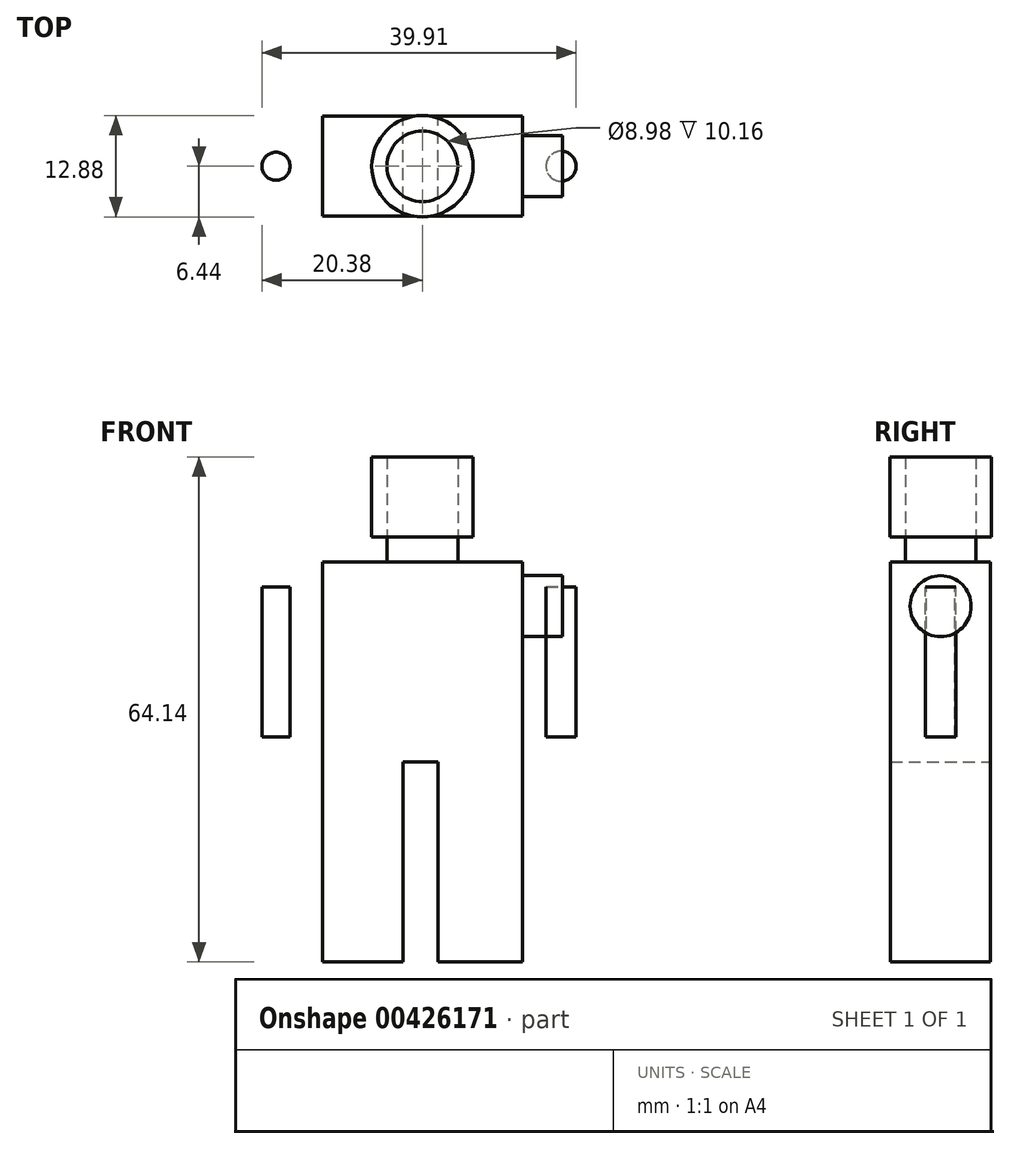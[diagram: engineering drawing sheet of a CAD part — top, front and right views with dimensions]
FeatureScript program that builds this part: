
annotation { "Feature Type Name" : "Feature", "Feature Type Description" : "" }
export const myFeature = defineFeature(function(context is Context, id is Id, definition is map)
    precondition{}
    {
        {
            var Q0;
            Q0=qCreatedBy(makeId("Top.planeOp"),FACE);
            var sketch = newSketch(context, id + "F0", { "sketchPlane" : qUnion([Q0])});
            skLineSegment(sketch, "E0.bottom", {"start": v(0, 0) * mm, "end": v(-12.7, 0) * mm});
            skLineSegment(sketch, "E0.top", {"start": v(0, -6.35) * mm, "end": v(-12.7, -6.35) * mm});
            skLineSegment(sketch, "E0.left", {"start": v(0, 0) * mm, "end": v(0, -6.35) * mm});
            skLineSegment(sketch, "E0.right", {"start": v(-12.7, 0) * mm, "end": v(-12.7, -6.35) * mm});
            skLineSegment(sketch, "E1.top", {"start": v(0, 6.35) * mm, "end": v(-12.7, 6.35) * mm});
            skLineSegment(sketch, "E1.left", {"start": v(0, 0) * mm, "end": v(0, 6.35) * mm});
            skLineSegment(sketch, "E1.right", {"start": v(-12.7, 0) * mm, "end": v(-12.7, 6.35) * mm});
            skLineSegment(sketch, "E2.bottom", {"start": v(0, -6.35) * mm, "end": v(12.7, -6.35) * mm});
            skLineSegment(sketch, "E2.top", {"start": v(0, 0) * mm, "end": v(12.7, 0) * mm});
            skLineSegment(sketch, "E2.left", {"start": v(0, -6.35) * mm, "end": v(0, 0) * mm});
            skLineSegment(sketch, "E2.right", {"start": v(12.7, -6.35) * mm, "end": v(12.7, 0) * mm});
            skLineSegment(sketch, "E3.top", {"start": v(0, 6.35) * mm, "end": v(12.7, 6.35) * mm});
            skLineSegment(sketch, "E3.right", {"start": v(12.7, 0) * mm, "end": v(12.7, 6.35) * mm});
            skSolve(sketch);
        }
        {
            var Q0;
            Q0 = qSketchRegion(id + "F0", true);
            extrude(context, id + "F1", {"entities" : qUnion([Q0]), "endBound" : BoundingType.SYMMETRIC, "depth" : 25.4 * mm});
        }
        {
            var Q0;
            Q0=makeQuery(id+"F1.opExtrude","CAP_FACE",FACE,{"disambiguationData":[OSD([sQuery(id+"F0.wireOp",EDGE,"E0.top"),sQuery(id+"F0.wireOp",EDGE,"E0.right"),sQuery(id+"F0.wireOp",EDGE,"E1.top"),sQuery(id+"F0.wireOp",EDGE,"E1.right"),sQuery(id+"F0.wireOp",EDGE,"E2.bottom"),sQuery(id+"F0.wireOp",EDGE,"E2.right"),sQuery(id+"F0.wireOp",EDGE,"E3.top"),sQuery(id+"F0.wireOp",EDGE,"E3.right")])],"isStart":false});
            var sketch = newSketch(context, id + "F2", { "sketchPlane" : qUnion([Q0])});
            skCircle(sketch, "E4", {"center": v(0, 0) * mm, "radius": 4.5 * mm});
            skSolve(sketch);
        }
        {
            var Q0;
            Q0=makeQuery(id+"F2.imprint","IMPRINT",FACE,{"disambiguationData":[TD([[makeQuery(id+"F2.imprint","IMPRINT",EDGE,{"derivedFrom":sQuery(id+"F2.wireOp",EDGE,"E4")}),1.0]])]});
            extrude(context, id + "F3", {"entities" : qUnion([Q0]), "operationType" : NewBodyOperationType.ADD, "endBound" : BoundingType.SYMMETRIC, "depth" : 6.35 * mm});
        }
        {
            var Q0;
            Q0=makeQuery(id+"F3.opExtrude","CAP_FACE",FACE,{"disambiguationData":[OSD([sQuery(id+"F2.wireOp",EDGE,"E4")])],"isStart":false});
            var sketch = newSketch(context, id + "F4", { "sketchPlane" : qUnion([Q0])});
            skCircle(sketch, "E5", {"center": v(0, 0) * mm, "radius": 6.44 * mm});
            skSolve(sketch);
        }
        {
            var Q0;
            Q0=makeQuery(id+"F4.imprint","IMPRINT",FACE,{"disambiguationData":[TD([[makeQuery(id+"F4.imprint","IMPRINT",EDGE,{"derivedFrom":sQuery(id+"F4.wireOp",EDGE,"E5")}),1.0]])]});
            extrude(context, id + "F5", {"entities" : qUnion([Q0]), "depth" : 10.16 * mm});
        }
        {
            var Q0;
            Q0=makeQuery(id+"F1.opExtrude","SWEPT_FACE",FACE,{"disambiguationData":[OSD([sQuery(id+"F0.wireOp",EDGE,"E0.right"),sQuery(id+"F0.wireOp",EDGE,"E1.right")])]});
            var sketch = newSketch(context, id + "F6", { "sketchPlane" : qUnion([Q0])});
            skCircle(sketch, "E6", {"center": v(0, 7.1) * mm, "radius": 3.91 * mm});
            skSolve(sketch);
        }
        {
            var Q0;
            Q0=sQuery(id+"F6.wireOp",EDGE,"E6");
            extrude(context, id + "F7", {"bodyType" : ToolBodyType.SURFACE, "surfaceEntities" : qUnion([Q0]), "depth" : 5.08 * mm});
        }
        {
            var Q0;
            Q0=makeQuery(id+"F1.opExtrude","SWEPT_FACE",FACE,{"disambiguationData":[OSD([sQuery(id+"F0.wireOp",EDGE,"E2.right"),sQuery(id+"F0.wireOp",EDGE,"E3.right")])]});
            var sketch = newSketch(context, id + "F8", { "sketchPlane" : qUnion([Q0])});
            skCircle(sketch, "E7", {"center": v(0, 7.1) * mm, "radius": 3.87 * mm});
            skSolve(sketch);
        }
        {
            var Q0;
            Q0 = qSketchRegion(id + "F8", true);
            extrude(context, id + "F9", {"entities" : qUnion([Q0]), "operationType" : NewBodyOperationType.ADD, "depth" : 5.08 * mm});
        }
        {
            var Q0;
            Q0=makeQuery(id+"F1.opExtrude","CAP_FACE",FACE,{"disambiguationData":[OSD([sQuery(id+"F0.wireOp",EDGE,"E0.top"),sQuery(id+"F0.wireOp",EDGE,"E0.right"),sQuery(id+"F0.wireOp",EDGE,"E1.top"),sQuery(id+"F0.wireOp",EDGE,"E1.right"),sQuery(id+"F0.wireOp",EDGE,"E2.bottom"),sQuery(id+"F0.wireOp",EDGE,"E2.right"),sQuery(id+"F0.wireOp",EDGE,"E3.top"),sQuery(id+"F0.wireOp",EDGE,"E3.right")])],"isStart":true});
            var sketch = newSketch(context, id + "F10", { "sketchPlane" : qUnion([Q0])});
            skLineSegment(sketch, "E8.bottom", {"start": v(-12.7, 6.35) * mm, "end": v(-2.45, 6.35) * mm});
            skLineSegment(sketch, "E8.top", {"start": v(-12.7, -6.35) * mm, "end": v(-2.45, -6.35) * mm});
            skLineSegment(sketch, "E8.left", {"start": v(-12.7, 6.35) * mm, "end": v(-12.7, -6.35) * mm});
            skLineSegment(sketch, "E8.right", {"start": v(-2.45, 6.35) * mm, "end": v(-2.45, -6.35) * mm});
            skLineSegment(sketch, "E9.bottom", {"start": v(12.7, 6.35) * mm, "end": v(1.96, 6.35) * mm});
            skLineSegment(sketch, "E9.top", {"start": v(12.7, -6.35) * mm, "end": v(1.96, -6.35) * mm});
            skLineSegment(sketch, "E9.left", {"start": v(12.7, 6.35) * mm, "end": v(12.7, -6.35) * mm});
            skLineSegment(sketch, "E9.right", {"start": v(1.96, 6.35) * mm, "end": v(1.96, -6.35) * mm});
            skSolve(sketch);
        }
        {
            var Q0;
            Q0=makeQuery(id+"F10.imprint","IMPRINT",FACE,{"disambiguationData":[TD([[makeQuery(id+"F10.imprint","IMPRINT",EDGE,{"derivedFrom":sQuery(id+"F10.wireOp",EDGE,"E8.bottom")}),1.0]])]});
            var Q1;
            Q1=makeQuery(id+"F10.imprint","IMPRINT",FACE,{"disambiguationData":[TD([[makeQuery(id+"F10.imprint","IMPRINT",EDGE,{"derivedFrom":sQuery(id+"F10.wireOp",EDGE,"E9.bottom")}),1.0]])]});
            extrude(context, id + "F11", {"entities" : qUnion([Q0, Q1]), "operationType" : NewBodyOperationType.ADD, "depth" : 25.4 * mm});
        }
        {
            var Q0;
            Q0=qCreatedBy(makeId("Top.planeOp"),FACE);
            var sketch = newSketch(context, id + "F12", { "sketchPlane" : qUnion([Q0])});
            skCircle(sketch, "E10", {"center": v(-18.6, 0) * mm, "radius": 1.78 * mm});
            skCircle(sketch, "E11", {"center": v(17.62, 0) * mm, "radius": 1.91 * mm});
            skSolve(sketch);
        }
        {
            var Q0;
            Q0 = qSketchRegion(id + "F12", true);
            extrude(context, id + "F13", {"entities" : qUnion([Q0]), "endBound" : BoundingType.SYMMETRIC, "oppositeDirection" : true, "depth" : 19.05 * mm});
        }
    });
